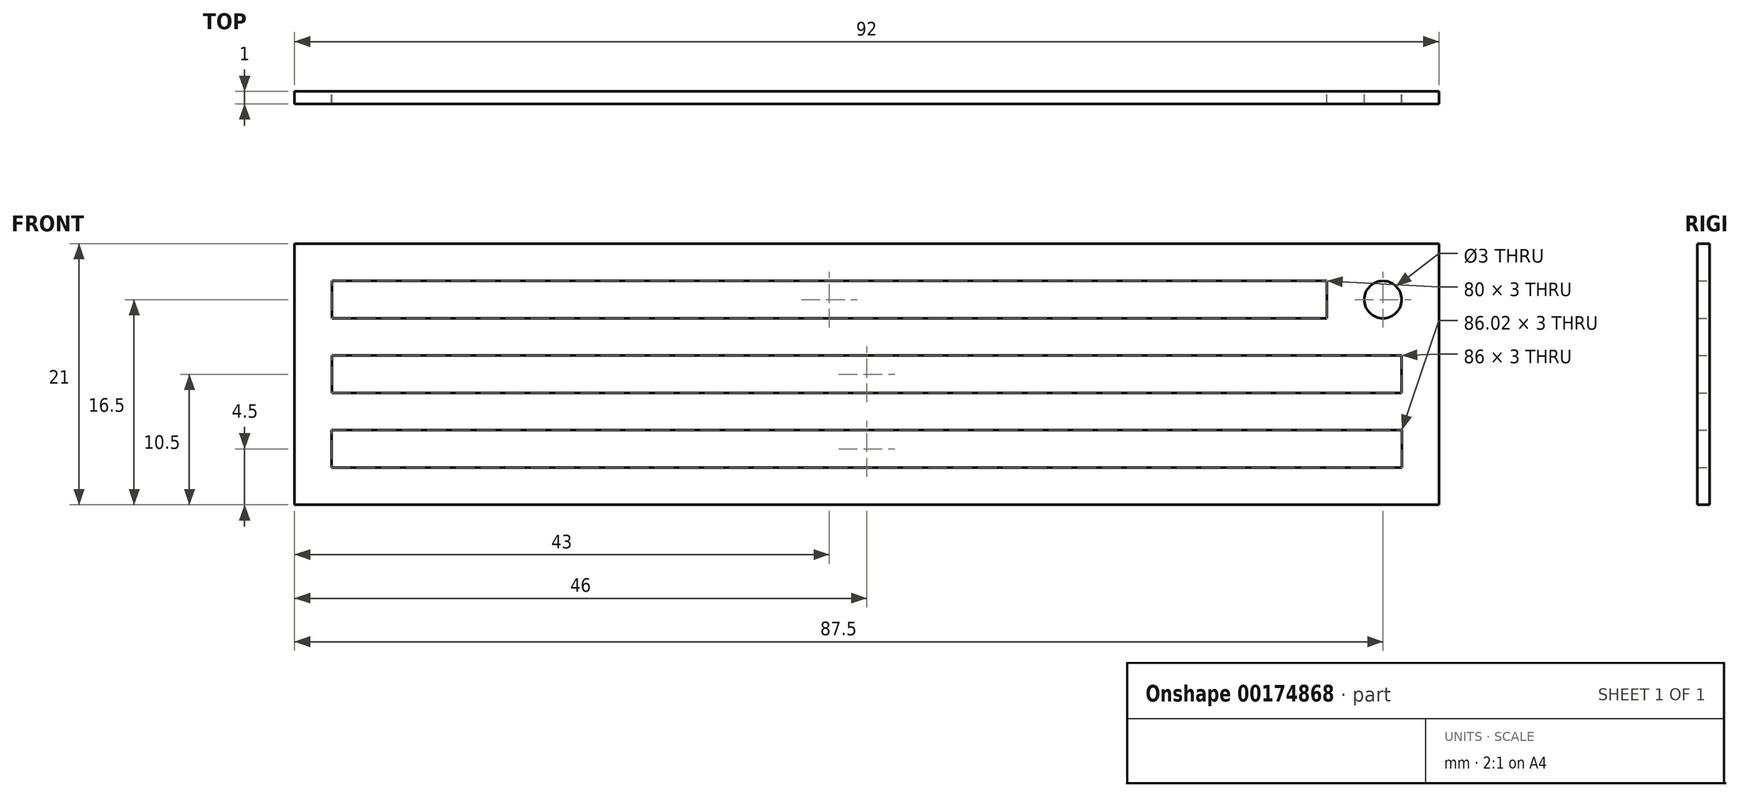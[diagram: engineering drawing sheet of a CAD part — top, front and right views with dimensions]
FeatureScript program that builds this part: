
annotation { "Feature Type Name" : "Feature", "Feature Type Description" : "" }
export const myFeature = defineFeature(function(context is Context, id is Id, definition is map)
    precondition{}
    {
        {
            var Q0;
            Q0=qCreatedBy(makeId("Front.planeOp"),FACE);
            var sketch = newSketch(context, id + "F0", { "sketchPlane" : qUnion([Q0])});
            skLineSegment(sketch, "E0.bottom", {"start": v(46, 10.5) * mm, "end": v(-46, 10.5) * mm});
            skLineSegment(sketch, "E0.top", {"start": v(46, -10.5) * mm, "end": v(-46, -10.5) * mm});
            skLineSegment(sketch, "E0.left", {"start": v(46, 10.5) * mm, "end": v(46, -10.5) * mm});
            skLineSegment(sketch, "E0.right", {"start": v(-46, 10.5) * mm, "end": v(-46, -10.5) * mm});
            skPoint(sketch, "E0.middle", {"position": v(0, 0) * mm});
            skLineSegment(sketch, "E1.bottom", {"start": v(43, 1.5) * mm, "end": v(-43, 1.5) * mm});
            skLineSegment(sketch, "E1.top", {"start": v(43, -1.5) * mm, "end": v(-43, -1.5) * mm});
            skLineSegment(sketch, "E1.left", {"start": v(43, 1.5) * mm, "end": v(43, -1.5) * mm});
            skLineSegment(sketch, "E1.right", {"start": v(-43, 1.5) * mm, "end": v(-43, -1.5) * mm});
            skLineSegment(sketch, "E2.bottom", {"start": v(43.01, -4.5) * mm, "end": v(-43.01, -4.5) * mm});
            skLineSegment(sketch, "E2.top", {"start": v(43.01, -7.5) * mm, "end": v(-43.01, -7.5) * mm});
            skLineSegment(sketch, "E2.left", {"start": v(43.01, -4.5) * mm, "end": v(43.01, -7.5) * mm});
            skLineSegment(sketch, "E2.right", {"start": v(-43.01, -4.5) * mm, "end": v(-43.01, -7.5) * mm});
            skPoint(sketch, "E2.middle", {"position": v(0, -6) * mm});
            skLineSegment(sketch, "E3.bottom", {"start": v(-43, 4.5) * mm, "end": v(37, 4.5) * mm});
            skLineSegment(sketch, "E3.top", {"start": v(-43, 7.5) * mm, "end": v(37, 7.5) * mm});
            skLineSegment(sketch, "E3.left", {"start": v(-43, 4.5) * mm, "end": v(-43, 7.5) * mm});
            skLineSegment(sketch, "E3.right", {"start": v(37, 4.5) * mm, "end": v(37, 7.5) * mm});
            skCircle(sketch, "E4", {"center": v(41.5, 6) * mm, "radius": 1.5 * mm});
            skSolve(sketch);
        }
        {
            var Q0;
            Q0=qSketchRegion(id+"F0",true);
            extrude(context, id + "F1", {"entities" : qUnion([Q0]), "depth" : 1 * mm});
        }
    });
